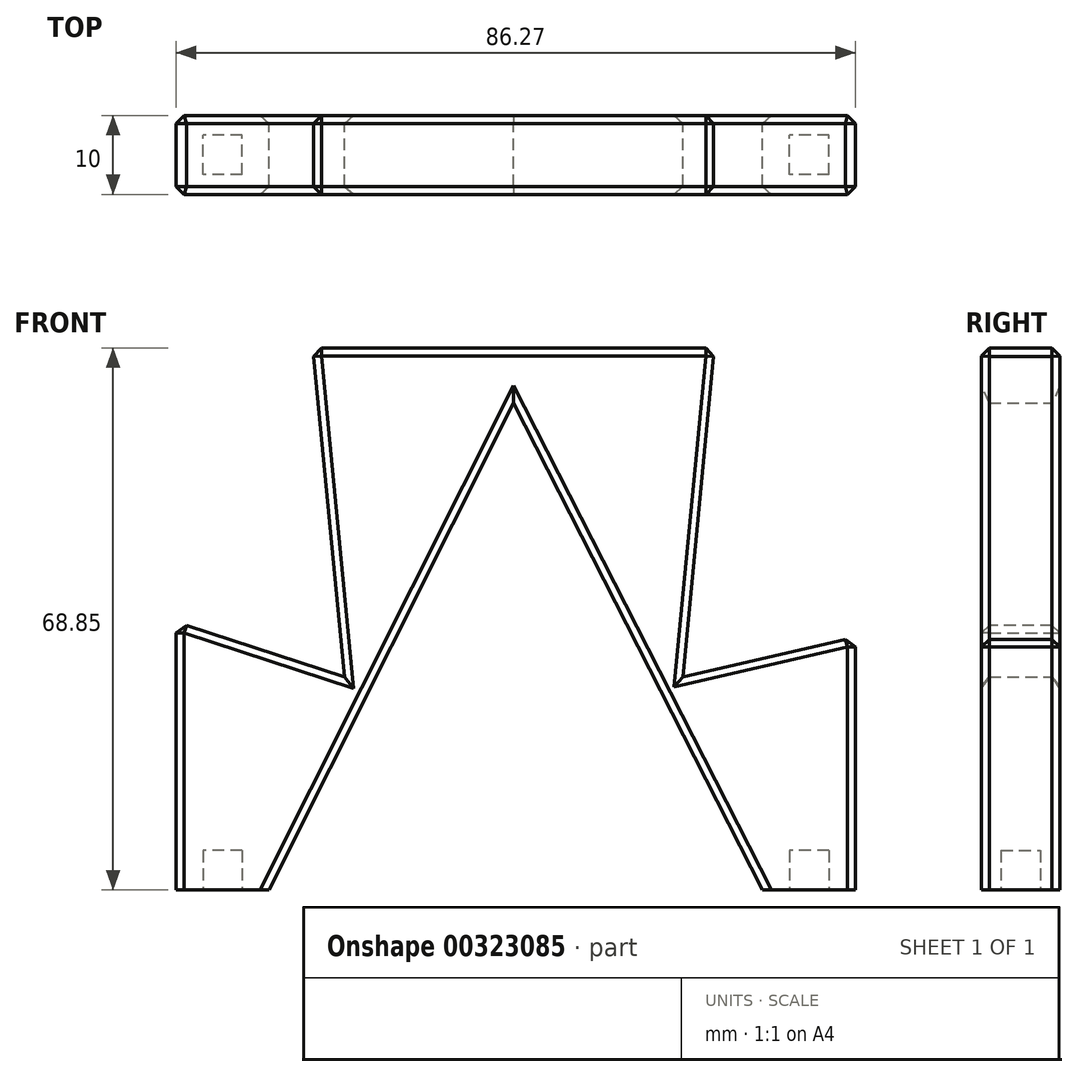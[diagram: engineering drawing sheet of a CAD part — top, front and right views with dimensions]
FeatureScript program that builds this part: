
annotation { "Feature Type Name" : "Feature", "Feature Type Description" : "" }
export const myFeature = defineFeature(function(context is Context, id is Id, definition is map)
    precondition{}
    {
        {
            var Q0;
            Q0=qCreatedBy(makeId("Front.planeOp"),FACE);
            var sketch = newSketch(context, id + "F0", { "sketchPlane" : qUnion([Q0])});
            skLineSegment(sketch, "E0", {"start": v(31.3, 27.04) * mm, "end": v(35.33, 68.85) * mm});
            skLineSegment(sketch, "E1", {"start": v(35.33, 68.85) * mm, "end": v(-15.67, 68.85) * mm});
            skLineSegment(sketch, "E2", {"start": v(-15.67, 68.85) * mm, "end": v(-11.65, 27.04) * mm});
            skLineSegment(sketch, "E3", {"start": v(-33.04, 34) * mm, "end": v(-33.04, 0) * mm});
            skLineSegment(sketch, "E4", {"start": v(-33.04, 0) * mm, "end": v(-21.24, 0) * mm});
            skPoint(sketch, "E5.startSnap0", {"position": v(9.83, 68.85) * mm});
            skLineSegment(sketch, "E6", {"start": v(-11.65, 27.04) * mm, "end": v(-33.04, 34) * mm});
            skLineSegment(sketch, "E7", {"start": v(-21.24, 0) * mm, "end": v(9.83, 61.85) * mm});
            skLineSegment(sketch, "E8", {"start": v(31.3, 27.04) * mm, "end": v(53.23, 32.1) * mm});
            skLineSegment(sketch, "E9", {"start": v(53.23, 32.1) * mm, "end": v(53.23, 0) * mm});
            skLineSegment(sketch, "E10", {"start": v(53.23, 0) * mm, "end": v(41.43, 0) * mm});
            skLineSegment(sketch, "E11", {"start": v(9.83, 61.85) * mm, "end": v(41.43, 0) * mm});
            skSolve(sketch);
        }
        {
            var Q0;
            Q0=makeQuery(id+"F0.imprint","IMPRINT",FACE,{"disambiguationData":[TD([[makeQuery(id+"F0.imprint","IMPRINT",EDGE,{"derivedFrom":sQuery(id+"F0.wireOp",EDGE,"E0")}),1.0]])]});
            extrude(context, id + "F1", {"entities" : qUnion([Q0]), "depth" : 10 * mm});
        }
        {
            var Q0;
            Q0=makeQuery(id+"F1.opExtrude","CAP_EDGE",EDGE,{"disambiguationData":[OSD([sQuery(id+"F0.wireOp",EDGE,"E1")])],"isStart":false});
            var Q1;
            Q1=makeQuery(id+"F1.opExtrude","CAP_EDGE",EDGE,{"disambiguationData":[OSD([sQuery(id+"F0.wireOp",EDGE,"E1")])],"isStart":true});
            var Q2;
            Q2=makeQuery(id+"F1.opExtrude","CAP_EDGE",EDGE,{"disambiguationData":[OSD([sQuery(id+"F0.wireOp",EDGE,"E2")])],"isStart":false});
            var Q3;
            Q3=makeQuery(id+"F1.opExtrude","CAP_EDGE",EDGE,{"disambiguationData":[OSD([sQuery(id+"F0.wireOp",EDGE,"E0")])],"isStart":false});
            var Q4;
            Q4=makeQuery(id+"F1.opExtrude","CAP_EDGE",EDGE,{"disambiguationData":[OSD([sQuery(id+"F0.wireOp",EDGE,"E8")])],"isStart":false});
            var Q5;
            Q5=makeQuery(id+"F1.opExtrude","CAP_EDGE",EDGE,{"disambiguationData":[OSD([sQuery(id+"F0.wireOp",EDGE,"E8")])],"isStart":true});
            var Q6;
            Q6=makeQuery(id+"F1.opExtrude","CAP_EDGE",EDGE,{"disambiguationData":[OSD([sQuery(id+"F0.wireOp",EDGE,"E9")])],"isStart":false});
            var Q7;
            Q7=makeQuery(id+"F1.opExtrude","CAP_EDGE",EDGE,{"disambiguationData":[OSD([sQuery(id+"F0.wireOp",EDGE,"E3")])],"isStart":false});
            var Q8;
            Q8=makeQuery(id+"F1.opExtrude","CAP_EDGE",EDGE,{"disambiguationData":[OSD([sQuery(id+"F0.wireOp",EDGE,"E6")])],"isStart":false});
            var Q9;
            Q9=makeQuery(id+"F1.opExtrude","CAP_EDGE",EDGE,{"disambiguationData":[OSD([sQuery(id+"F0.wireOp",EDGE,"E11")])],"isStart":false});
            var Q10;
            Q10=makeQuery(id+"F1.opExtrude","CAP_EDGE",EDGE,{"disambiguationData":[OSD([sQuery(id+"F0.wireOp",EDGE,"E7")])],"isStart":false});
            var Q11;
            Q11=makeQuery(id+"F1.opExtrude","CAP_EDGE",EDGE,{"disambiguationData":[OSD([sQuery(id+"F0.wireOp",EDGE,"E2")])],"isStart":true});
            var Q12;
            Q12=makeQuery(id+"F1.opExtrude","CAP_EDGE",EDGE,{"disambiguationData":[OSD([sQuery(id+"F0.wireOp",EDGE,"E0")])],"isStart":true});
            var Q13;
            Q13=makeQuery(id+"F1.opExtrude","CAP_EDGE",EDGE,{"disambiguationData":[OSD([sQuery(id+"F0.wireOp",EDGE,"E11")])],"isStart":true});
            var Q14;
            Q14=makeQuery(id+"F1.opExtrude","CAP_EDGE",EDGE,{"disambiguationData":[OSD([sQuery(id+"F0.wireOp",EDGE,"E7")])],"isStart":true});
            var Q15;
            Q15=makeQuery(id+"F1.opExtrude","CAP_EDGE",EDGE,{"disambiguationData":[OSD([sQuery(id+"F0.wireOp",EDGE,"E6")])],"isStart":true});
            var Q16;
            Q16=makeQuery(id+"F1.opExtrude","SWEPT_EDGE",EDGE,{"disambiguationData":[OSD([sQuery(id+"F0.wireOp",EDGE,"E3"),sQuery(id+"F0.wireOp",EDGE,"E6")])]});
            var Q17;
            Q17=makeQuery(id+"F1.opExtrude","SWEPT_EDGE",EDGE,{"disambiguationData":[OSD([sQuery(id+"F0.wireOp",EDGE,"E1"),sQuery(id+"F0.wireOp",EDGE,"E2")])]});
            var Q18;
            Q18=makeQuery(id+"F1.opExtrude","SWEPT_EDGE",EDGE,{"disambiguationData":[OSD([sQuery(id+"F0.wireOp",EDGE,"E0"),sQuery(id+"F0.wireOp",EDGE,"E1")])]});
            var Q19;
            Q19=makeQuery(id+"F1.opExtrude","CAP_EDGE",EDGE,{"disambiguationData":[OSD([sQuery(id+"F0.wireOp",EDGE,"E3")])],"isStart":true});
            var Q20;
            Q20=makeQuery(id+"F1.opExtrude","CAP_EDGE",EDGE,{"disambiguationData":[OSD([sQuery(id+"F0.wireOp",EDGE,"E9")])],"isStart":true});
            var Q21;
            Q21=makeQuery(id+"F1.opExtrude","SWEPT_EDGE",EDGE,{"disambiguationData":[OSD([sQuery(id+"F0.wireOp",EDGE,"E8"),sQuery(id+"F0.wireOp",EDGE,"E9")])]});
            chamfer(context, id + "F2", {"entities" : qUnion([Q0, Q1, Q2, Q3, Q4, Q5, Q6, Q7, Q8, Q9, Q10, Q11, Q12, Q13, Q14, Q15, Q16, Q17, Q18, Q19, Q20, Q21]), "width" : 1 * mm, "tangentPropagation" : true});
        }
        {
            var Q0;
            Q0=makeQuery(id+"F1.opExtrude","SWEPT_FACE",FACE,{"disambiguationData":[OSD([sQuery(id+"F0.wireOp",EDGE,"E4")])]});
            var sketch = newSketch(context, id + "F3", { "sketchPlane" : qUnion([Q0])});
            skPoint(sketch, "E12", {"position": v(-27.2, 10) * mm});
            skLineSegment(sketch, "E13.bottom", {"start": v(-24.53, 5) * mm, "end": v(-29.75, 5) * mm});
            skLineSegment(sketch, "E13.top", {"start": v(-24.53, 5) * mm, "end": v(-29.75, 5) * mm});
            skLineSegment(sketch, "E13.left", {"start": v(-24.53, 5) * mm, "end": v(-24.53, 5) * mm});
            skLineSegment(sketch, "E13.right", {"start": v(-29.75, 5) * mm, "end": v(-29.75, 5) * mm});
            skPoint(sketch, "E13.middle", {"position": v(-27.14, 5) * mm});
            skLineSegment(sketch, "E14.bottom", {"start": v(-24.64, 7.5) * mm, "end": v(-29.64, 7.5) * mm});
            skLineSegment(sketch, "E14.top", {"start": v(-24.64, 2.5) * mm, "end": v(-29.64, 2.5) * mm});
            skLineSegment(sketch, "E14.left", {"start": v(-24.64, 7.5) * mm, "end": v(-24.64, 2.5) * mm});
            skLineSegment(sketch, "E14.right", {"start": v(-29.64, 7.5) * mm, "end": v(-29.64, 2.5) * mm});
            skSolve(sketch);
        }
        {
            var Q0;
            Q0 = qSketchRegion(id + "F3", true);
            extrude(context, id + "F4", {"entities" : qUnion([Q0]), "operationType" : NewBodyOperationType.REMOVE, "oppositeDirection" : true, "depth" : 5 * mm});
        }
        {
            var Q0;
            Q0=makeQuery(id+"F1.opExtrude","SWEPT_FACE",FACE,{"disambiguationData":[OSD([sQuery(id+"F0.wireOp",EDGE,"E10")])]});
            var sketch = newSketch(context, id + "F5", { "sketchPlane" : qUnion([Q0])});
            skPoint(sketch, "E15", {"position": v(47.39, 10) * mm});
            skPoint(sketch, "E16", {"position": v(47.39, 0) * mm});
            skPoint(sketch, "E17", {"position": v(41.43, 5) * mm});
            skPoint(sketch, "E18", {"position": v(53.23, 5) * mm});
            skLineSegment(sketch, "E19", {"start": v(47.39, 10) * mm, "end": v(47.39, 0) * mm});
            skLineSegment(sketch, "E20", {"start": v(41.43, 5) * mm, "end": v(53.23, 5) * mm});
            skPoint(sketch, "E21", {"position": v(47.39, 5) * mm});
            skLineSegment(sketch, "E22.bottom", {"start": v(49.89, 7.5) * mm, "end": v(44.89, 7.5) * mm});
            skLineSegment(sketch, "E22.top", {"start": v(49.89, 2.5) * mm, "end": v(44.89, 2.5) * mm});
            skLineSegment(sketch, "E22.left", {"start": v(49.89, 7.5) * mm, "end": v(49.89, 2.5) * mm});
            skLineSegment(sketch, "E22.right", {"start": v(44.89, 7.5) * mm, "end": v(44.89, 2.5) * mm});
            skSolve(sketch);
        }
        {
            var Q0;
            {var subQ0=sQuery(id+"F5.wireOp",EDGE,"E20");var subQ1=sQuery(id+"F5.wireOp",EDGE,"E19");var subQ2=makeQuery(id+"F5.imprint","INTERSECT",VERTEX,{"derivedFrom":[subQ1,subQ0]});Q0=makeQuery(id+"F5.imprint","IMPRINT",FACE,{"disambiguationData":[TD([[makeQuery(id+"F5.imprint","IMPRINT",EDGE,{"disambiguationData":[TD([[subQ2,-1.0]])],"derivedFrom":subQ1}),1.0]])]});}
            var Q1;
            {var subQ0=sQuery(id+"F5.wireOp",EDGE,"E22.bottom");var subQ1=sQuery(id+"F5.wireOp",EDGE,"E19");var subQ2=makeQuery(id+"F5.imprint","INTERSECT",VERTEX,{"derivedFrom":[subQ1,subQ0]});Q1=makeQuery(id+"F5.imprint","IMPRINT",FACE,{"disambiguationData":[TD([[makeQuery(id+"F5.imprint","IMPRINT",EDGE,{"disambiguationData":[TD([[subQ2,-1.0]])],"derivedFrom":subQ1}),-1.0]])]});}
            var Q2;
            {var subQ0=sQuery(id+"F5.wireOp",EDGE,"E20");var subQ1=sQuery(id+"F5.wireOp",EDGE,"E19");var subQ2=makeQuery(id+"F5.imprint","INTERSECT",VERTEX,{"derivedFrom":[subQ1,subQ0]});Q2=makeQuery(id+"F5.imprint","IMPRINT",FACE,{"disambiguationData":[TD([[makeQuery(id+"F5.imprint","IMPRINT",EDGE,{"disambiguationData":[TD([[subQ2,-1.0]])],"derivedFrom":subQ1}),-1.0]])]});}
            var Q3;
            {var subQ0=sQuery(id+"F5.wireOp",EDGE,"E22.bottom");var subQ1=sQuery(id+"F5.wireOp",EDGE,"E19");var subQ2=makeQuery(id+"F5.imprint","INTERSECT",VERTEX,{"derivedFrom":[subQ1,subQ0]});Q3=makeQuery(id+"F5.imprint","IMPRINT",FACE,{"disambiguationData":[TD([[makeQuery(id+"F5.imprint","IMPRINT",EDGE,{"disambiguationData":[TD([[subQ2,-1.0]])],"derivedFrom":subQ1}),1.0]])]});}
            extrude(context, id + "F6", {"entities" : qUnion([Q0, Q1, Q2, Q3]), "operationType" : NewBodyOperationType.REMOVE, "oppositeDirection" : true, "depth" : 5 * mm});
        }
    });
